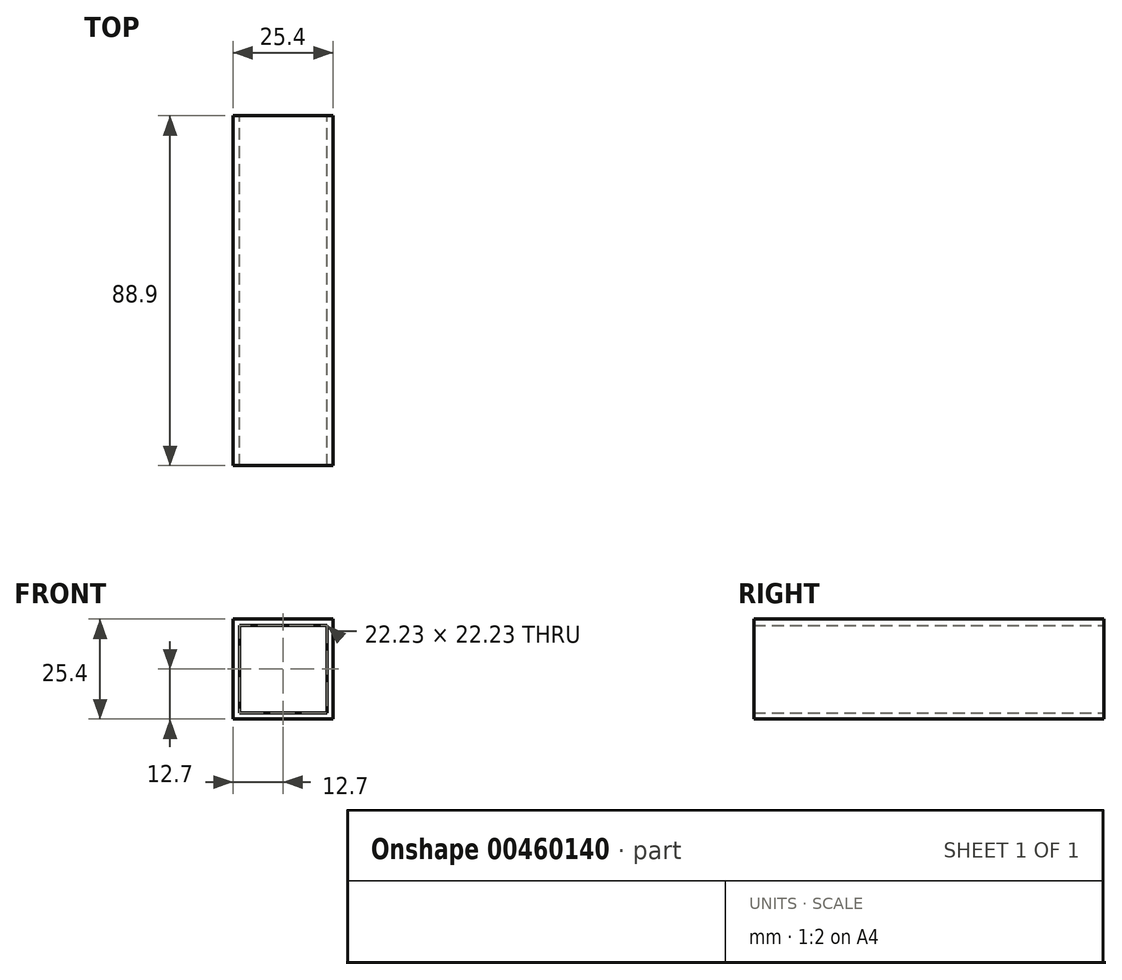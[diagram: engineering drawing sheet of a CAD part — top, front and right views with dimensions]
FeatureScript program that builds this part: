
annotation { "Feature Type Name" : "Feature", "Feature Type Description" : "" }
export const myFeature = defineFeature(function(context is Context, id is Id, definition is map)
    precondition{}
    {
        {
            var Q0;
            Q0=qCreatedBy(makeId("Front.planeOp"),FACE);
            var sketch = newSketch(context, id + "F0", { "sketchPlane" : qUnion([Q0])});
            skLineSegment(sketch, "E0.bottom", {"start": v(12.7, 12.7) * mm, "end": v(-12.7, 12.7) * mm});
            skLineSegment(sketch, "E0.top", {"start": v(12.7, -12.7) * mm, "end": v(-12.7, -12.7) * mm});
            skLineSegment(sketch, "E0.left", {"start": v(12.7, 12.7) * mm, "end": v(12.7, -12.7) * mm});
            skLineSegment(sketch, "E0.right", {"start": v(-12.7, 12.7) * mm, "end": v(-12.7, -12.7) * mm});
            skPoint(sketch, "E0.middle", {"position": v(0, 0) * mm});
            skLineSegment(sketch, "E1.bottom", {"start": v(11.11, 11.11) * mm, "end": v(-11.11, 11.11) * mm});
            skLineSegment(sketch, "E1.top", {"start": v(11.11, -11.11) * mm, "end": v(-11.11, -11.11) * mm});
            skLineSegment(sketch, "E1.left", {"start": v(11.11, 11.11) * mm, "end": v(11.11, -11.11) * mm});
            skLineSegment(sketch, "E1.right", {"start": v(-11.11, 11.11) * mm, "end": v(-11.11, -11.11) * mm});
            skSolve(sketch);
        }
        {
            var Q0;
            Q0=makeQuery(id+"F0.imprint","IMPRINT",FACE,{"disambiguationData":[TD([[makeQuery(id+"F0.imprint","IMPRINT",EDGE,{"derivedFrom":sQuery(id+"F0.wireOp",EDGE,"E0.bottom")}),1.0]])]});
            extrude(context, id + "F1", {"entities" : qUnion([Q0]), "depth" : 88.9 * mm});
        }
    });
